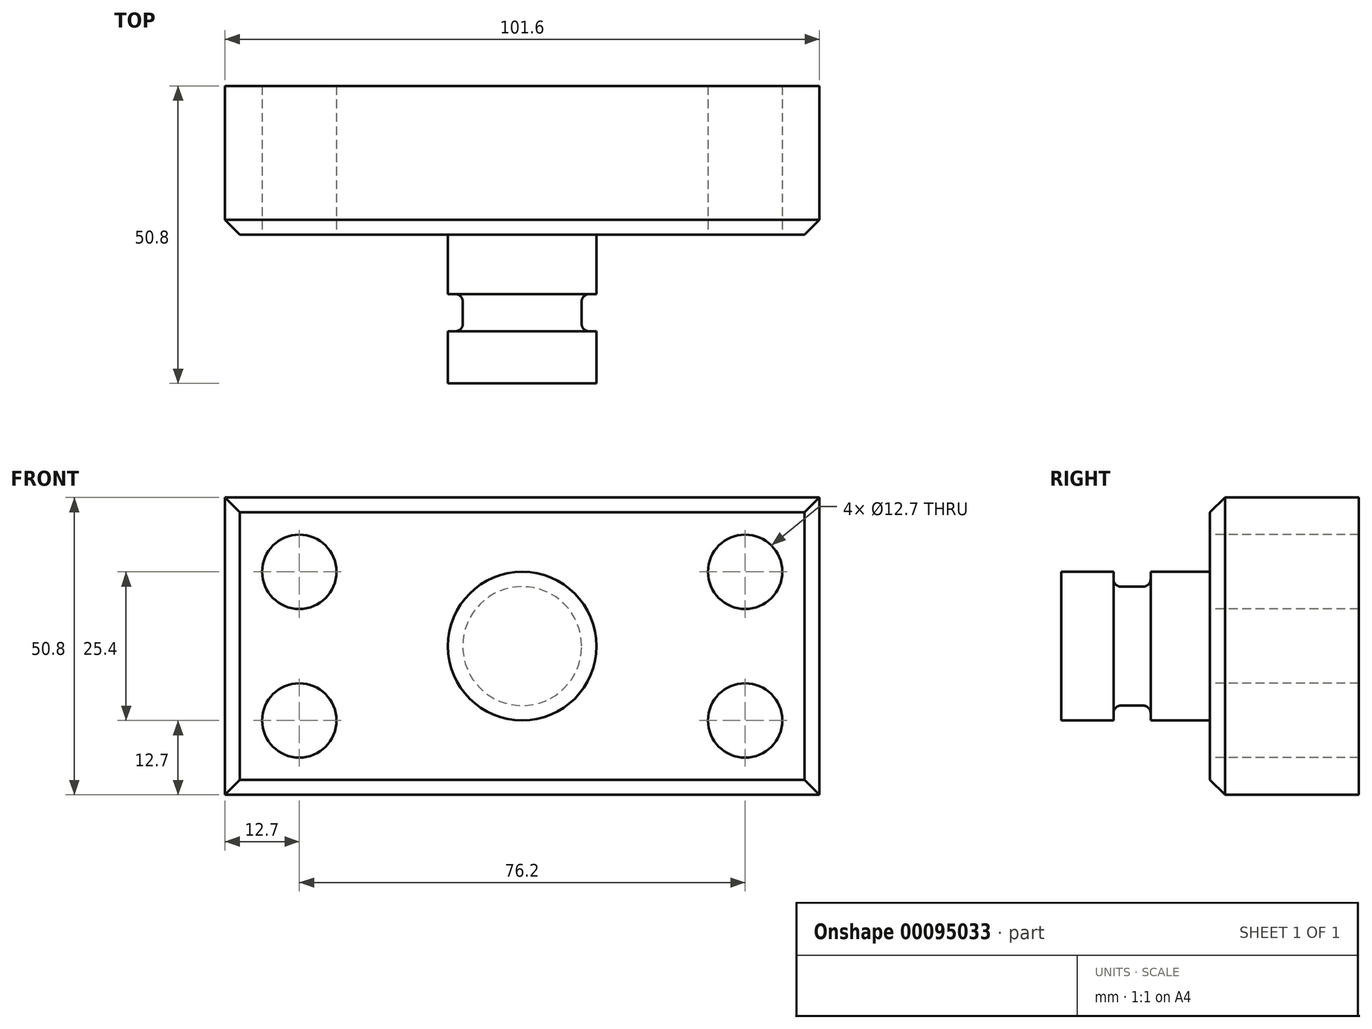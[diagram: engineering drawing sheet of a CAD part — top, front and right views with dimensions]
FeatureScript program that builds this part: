
annotation { "Feature Type Name" : "Feature", "Feature Type Description" : "" }
export const myFeature = defineFeature(function(context is Context, id is Id, definition is map)
    precondition{}
    {
        {
            var Q0;
            Q0=qCreatedBy(makeId("Front.planeOp"),FACE);
            var sketch = newSketch(context, id + "F0", { "sketchPlane" : qUnion([Q0])});
            skLineSegment(sketch, "E0.bottom", {"start": v(50.8, 25.4) * mm, "end": v(-50.8, 25.4) * mm});
            skLineSegment(sketch, "E0.top", {"start": v(50.8, -25.4) * mm, "end": v(-50.8, -25.4) * mm});
            skLineSegment(sketch, "E0.left", {"start": v(50.8, 25.4) * mm, "end": v(50.8, -25.4) * mm});
            skLineSegment(sketch, "E0.right", {"start": v(-50.8, 25.4) * mm, "end": v(-50.8, -25.4) * mm});
            skPoint(sketch, "E0.middle", {"position": v(0, 0) * mm});
            skSolve(sketch);
        }
        {
            var Q0;
            Q0 = qSketchRegion(id + "F0", true);
            extrude(context, id + "F1", {"entities" : qUnion([Q0]), "depth" : 25.4 * mm});
        }
        {
            var Q0;
            Q0=makeQuery(id+"F1.opExtrude","CAP_FACE",FACE,{"disambiguationData":[OSD([sQuery(id+"F0.wireOp",EDGE,"E0.bottom"),sQuery(id+"F0.wireOp",EDGE,"E0.top"),sQuery(id+"F0.wireOp",EDGE,"E0.left"),sQuery(id+"F0.wireOp",EDGE,"E0.right")])],"isStart":false});
            var sketch = newSketch(context, id + "F2", { "sketchPlane" : qUnion([Q0])});
            skCircle(sketch, "E1", {"center": v(-38.1, 12.7) * mm, "radius": 6.35 * mm});
            skCircle(sketch, "E2", {"center": v(38.1, 12.7) * mm, "radius": 6.35 * mm});
            skCircle(sketch, "E3", {"center": v(38.1, -12.7) * mm, "radius": 6.35 * mm});
            skCircle(sketch, "E4", {"center": v(-38.1, -12.7) * mm, "radius": 6.35 * mm});
            skSolve(sketch);
        }
        {
            var Q0;
            Q0 = qSketchRegion(id + "F2", true);
            extrude(context, id + "F3", {"entities" : qUnion([Q0]), "operationType" : NewBodyOperationType.REMOVE, "endBound" : BoundingType.THROUGH_ALL, "oppositeDirection" : true, "depth" : 25.4 * mm});
        }
        {
            var Q0;
            Q0=qCreatedBy(makeId("Top.planeOp"),FACE);
            var sketch = newSketch(context, id + "F4", { "sketchPlane" : qUnion([Q0])});
            skLineSegment(sketch, "E5.bottom", {"start": v(0, -25.4) * mm, "end": v(12.7, -25.4) * mm});
            skLineSegment(sketch, "E5.top", {"start": v(0, -50.8) * mm, "end": v(12.7, -50.8) * mm});
            skLineSegment(sketch, "E5.left", {"start": v(0, -25.4) * mm, "end": v(0, -50.8) * mm});
            skLineSegment(sketch, "E5.right", {"start": v(12.7, -25.4) * mm, "end": v(12.7, -50.8) * mm});
            skSolve(sketch);
        }
        {
            var Q0;
            Q0 = qSketchRegion(id + "F4", true);
            var Q1;
            Q1=sQuery(id+"F4.wireOp",EDGE,"E5.left");
            revolve(context, id + "F5", {"operationType" : NewBodyOperationType.ADD, "entities" : qUnion([Q0]), "axis" : qUnion([Q1]), "revolveType" : RevolveType.FULL});
        }
        {
            var Q0;
            Q0=qCreatedBy(makeId("Top.planeOp"),FACE);
            var sketch = newSketch(context, id + "F6", { "sketchPlane" : qUnion([Q0])});
            skLineSegment(sketch, "E6.bottom", {"start": v(-44.88, -35.56) * mm, "end": v(-10.16, -35.56) * mm});
            skLineSegment(sketch, "E6.top", {"start": v(-44.88, -41.91) * mm, "end": v(-10.16, -41.91) * mm});
            skLineSegment(sketch, "E6.left", {"start": v(-44.88, -35.56) * mm, "end": v(-44.88, -41.91) * mm});
            skLineSegment(sketch, "E6.right", {"start": v(-10.16, -35.56) * mm, "end": v(-10.16, -41.91) * mm});
            skLineSegment(sketch, "E7", {"start": v(0, 0) * mm, "end": v(0, -80.94) * mm, "construction": true});
            skSolve(sketch);
        }
        {
            var Q0;
            Q0 = qSketchRegion(id + "F6", true);
            var Q1;
            Q1=sQuery(id+"F6.wireOp",EDGE,"E7");
            revolve(context, id + "F7", {"operationType" : NewBodyOperationType.REMOVE, "entities" : qUnion([Q0]), "axis" : qUnion([Q1]), "revolveType" : RevolveType.FULL, "oppositeDirection" : true});
        }
        {
            var Q0;
            Q0=makeQuery(id+"F5.opRevolve","SWEPT_EDGE",EDGE,{"disambiguationData":[OSD([sQuery(id+"F4.wireOp",EDGE,"E5.bottom"),sQuery(id+"F4.wireOp",EDGE,"E5.right")])]});
            var Q1;
            Q1=makeQuery(id+"F7.boolean.opBoolean","COPY",EDGE,{"derivedFrom":makeQuery(id+"F7.opRevolve","SWEPT_EDGE",EDGE,{"disambiguationData":[OSD([sQuery(id+"F6.wireOp",EDGE,"E6.bottom"),sQuery(id+"F6.wireOp",EDGE,"E6.right")])]})});
            var Q2;
            Q2=makeQuery(id+"F7.boolean.opBoolean","COPY",EDGE,{"derivedFrom":makeQuery(id+"F7.opRevolve","SWEPT_EDGE",EDGE,{"disambiguationData":[OSD([sQuery(id+"F6.wireOp",EDGE,"E6.top"),sQuery(id+"F6.wireOp",EDGE,"E6.right")])]})});
            fillet(context, id + "F8", {"entities" : qUnion([Q0, Q1, Q2]), "radius" : 1.27 * mm, "tangentPropagation" : true, "allowEdgeOverflow" : false});
        }
        {
            var Q0;
            Q0=makeQuery(id+"F1.opExtrude","CAP_EDGE",EDGE,{"disambiguationData":[OSD([sQuery(id+"F0.wireOp",EDGE,"E0.bottom")])],"isStart":false});
            var Q1;
            Q1=makeQuery(id+"F1.opExtrude","CAP_EDGE",EDGE,{"disambiguationData":[OSD([sQuery(id+"F0.wireOp",EDGE,"E0.left")])],"isStart":false});
            var Q2;
            Q2=makeQuery(id+"F1.opExtrude","CAP_EDGE",EDGE,{"disambiguationData":[OSD([sQuery(id+"F0.wireOp",EDGE,"E0.top")])],"isStart":false});
            var Q3;
            Q3=makeQuery(id+"F1.opExtrude","CAP_EDGE",EDGE,{"disambiguationData":[OSD([sQuery(id+"F0.wireOp",EDGE,"E0.right")])],"isStart":false});
            chamfer(context, id + "F9", {"entities" : qUnion([Q0, Q1, Q2, Q3]), "width" : 2.54 * mm, "tangentPropagation" : true});
        }
    });
